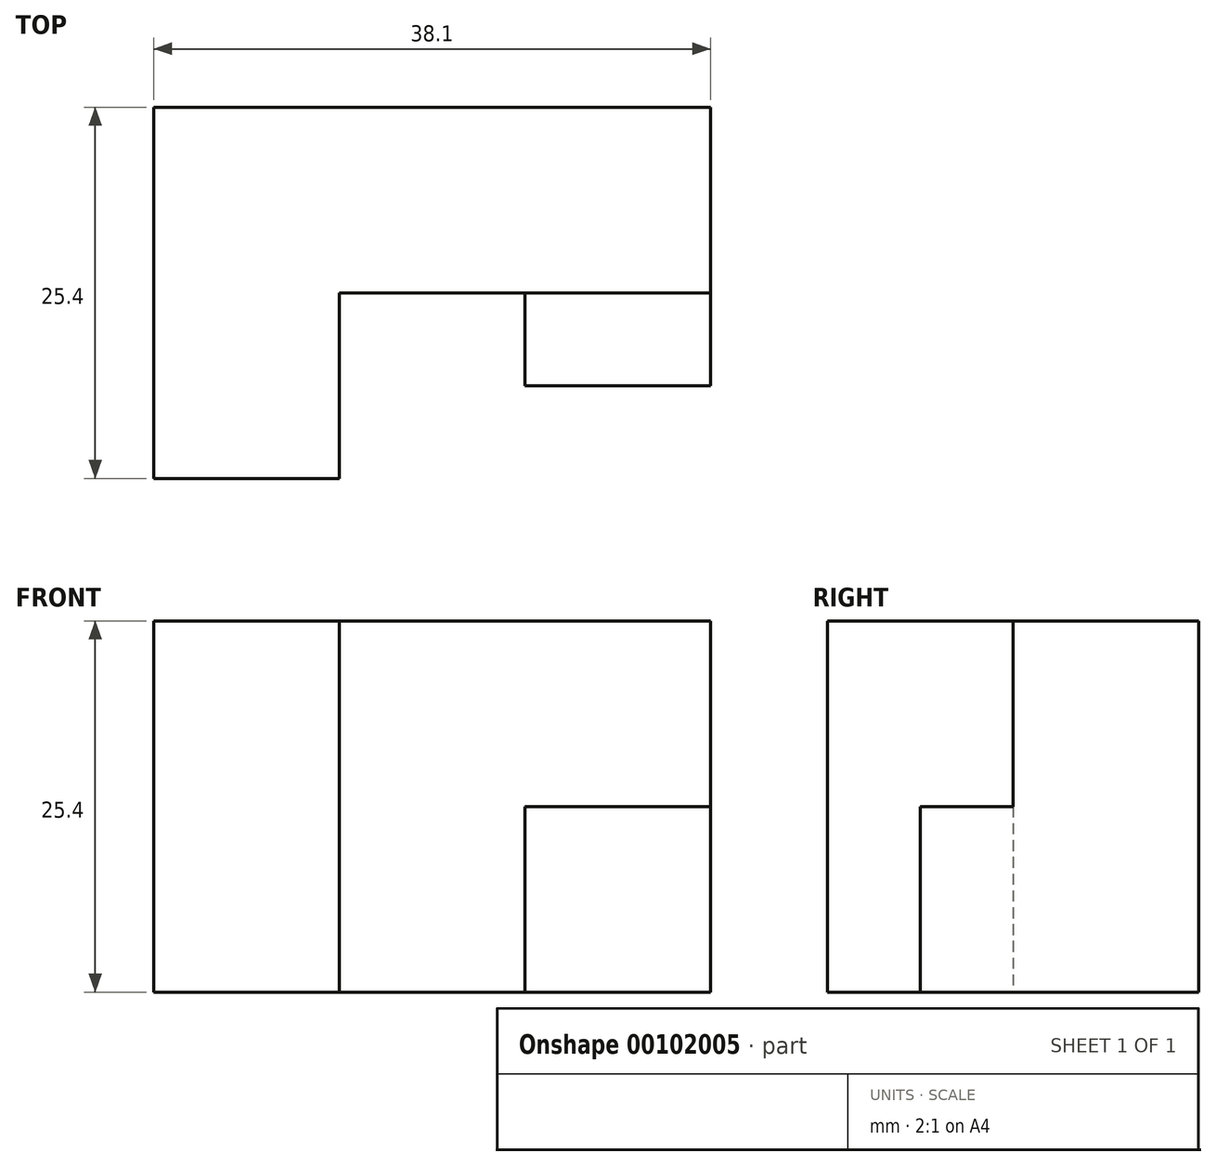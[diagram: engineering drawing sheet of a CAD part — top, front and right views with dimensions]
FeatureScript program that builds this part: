
annotation { "Feature Type Name" : "Feature", "Feature Type Description" : "" }
export const myFeature = defineFeature(function(context is Context, id is Id, definition is map)
    precondition{}
    {
        {
            var Q0;
            Q0=qCreatedBy(makeId("Front.planeOp"),FACE);
            var sketch = newSketch(context, id + "F0", { "sketchPlane" : qUnion([Q0])});
            skLineSegment(sketch, "E0.bottom", {"start": v(0, 0) * mm, "end": v(38.1, 0) * mm});
            skLineSegment(sketch, "E0.top", {"start": v(0, 25.4) * mm, "end": v(38.1, 25.4) * mm});
            skLineSegment(sketch, "E0.left", {"start": v(0, 0) * mm, "end": v(0, 25.4) * mm});
            skLineSegment(sketch, "E0.right", {"start": v(38.1, 0) * mm, "end": v(38.1, 25.4) * mm});
            skSolve(sketch);
        }
        {
            var Q0;
            Q0 = qSketchRegion(id + "F0", true);
            extrude(context, id + "F1", {"entities" : qUnion([Q0]), "depth" : 12.7 * mm});
        }
        {
            var Q0;
            Q0=qCreatedBy(makeId("Front.planeOp"),FACE);
            var sketch = newSketch(context, id + "F2", { "sketchPlane" : qUnion([Q0])});
            skLineSegment(sketch, "E1.bottom", {"start": v(0, 0) * mm, "end": v(12.7, 0) * mm});
            skLineSegment(sketch, "E1.top", {"start": v(0, 25.4) * mm, "end": v(12.7, 25.4) * mm});
            skLineSegment(sketch, "E1.left", {"start": v(0, 0) * mm, "end": v(0, 25.4) * mm});
            skLineSegment(sketch, "E1.right", {"start": v(12.7, 0) * mm, "end": v(12.7, 25.4) * mm});
            skSolve(sketch);
        }
        {
            var Q0;
            Q0 = qSketchRegion(id + "F2", true);
            extrude(context, id + "F3", {"entities" : qUnion([Q0]), "operationType" : NewBodyOperationType.ADD, "depth" : 25.4 * mm});
        }
        {
            var Q0;
            Q0=qCreatedBy(makeId("Front.planeOp"),FACE);
            var sketch = newSketch(context, id + "F4", { "sketchPlane" : qUnion([Q0])});
            skLineSegment(sketch, "E2.bottom", {"start": v(38.1, 0) * mm, "end": v(25.4, 0) * mm});
            skLineSegment(sketch, "E2.top", {"start": v(38.1, 12.7) * mm, "end": v(25.4, 12.7) * mm});
            skLineSegment(sketch, "E2.left", {"start": v(38.1, 0) * mm, "end": v(38.1, 12.7) * mm});
            skLineSegment(sketch, "E2.right", {"start": v(25.4, 0) * mm, "end": v(25.4, 12.7) * mm});
            skSolve(sketch);
        }
        {
            var Q0;
            Q0 = qSketchRegion(id + "F4", true);
            extrude(context, id + "F5", {"entities" : qUnion([Q0]), "operationType" : NewBodyOperationType.ADD, "depth" : 19.05 * mm});
        }
    });
